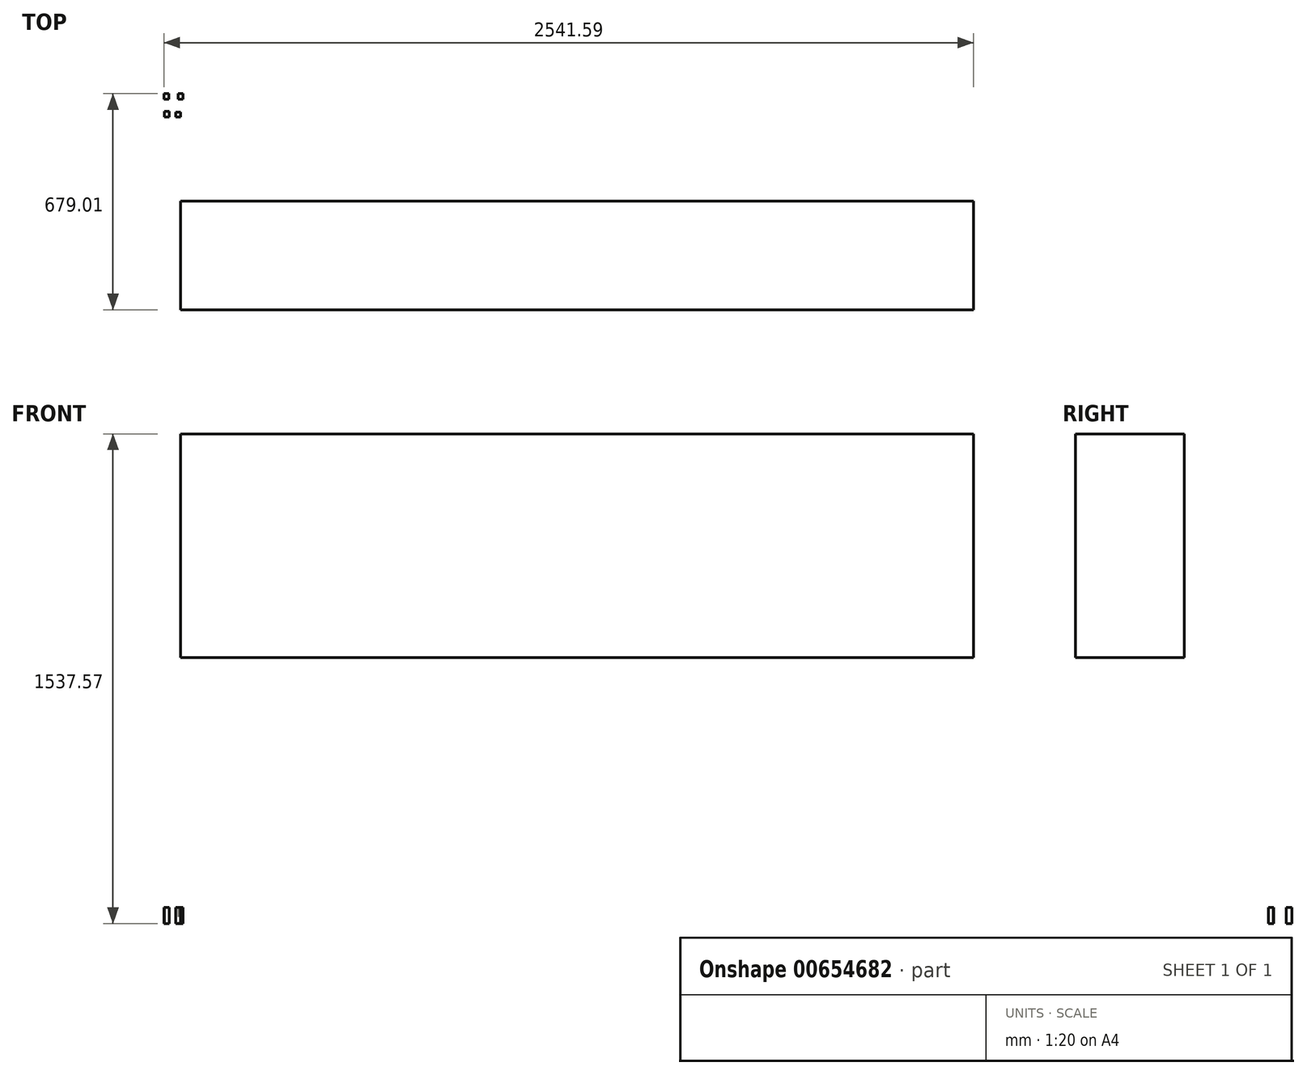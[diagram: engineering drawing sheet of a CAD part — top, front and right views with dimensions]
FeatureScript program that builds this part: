
annotation { "Feature Type Name" : "Feature", "Feature Type Description" : "" }
export const myFeature = defineFeature(function(context is Context, id is Id, definition is map)
    precondition{}
    {
        {
            var Q0;
            Q0=qCreatedBy(makeId("Top.planeOp"),FACE);
            var sketch = newSketch(context, id + "F0", { "sketchPlane" : qUnion([Q0])});
            skLineSegment(sketch, "E0.bottom", {"start": v(-51.02, -64.93) * mm, "end": v(-36.1, -64.93) * mm});
            skLineSegment(sketch, "E0.top", {"start": v(-51.02, -47.21) * mm, "end": v(-36.1, -47.21) * mm});
            skLineSegment(sketch, "E0.left", {"start": v(-51.02, -64.93) * mm, "end": v(-51.02, -47.21) * mm});
            skLineSegment(sketch, "E0.right", {"start": v(-36.1, -64.93) * mm, "end": v(-36.1, -47.21) * mm});
            skSolve(sketch);
        }
        {
            var Q0;
            Q0 = qSketchRegion(id + "F0", true);
            extrude(context, id + "F1", {"entities" : qUnion([Q0]), "depth" : 50.8 * mm, "offsetDistance" : 25.4 * mm});
        }
        {
            var Q0;
            Q0=qCreatedBy(makeId("Top.planeOp"),FACE);
            var sketch = newSketch(context, id + "F2", { "sketchPlane" : qUnion([Q0])});
            skLineSegment(sketch, "E1.bottom", {"start": v(-52.39, -8.86) * mm, "end": v(-37.46, -8.86) * mm});
            skLineSegment(sketch, "E1.top", {"start": v(-52.39, 8.86) * mm, "end": v(-37.46, 8.86) * mm});
            skLineSegment(sketch, "E1.left", {"start": v(-52.39, -8.86) * mm, "end": v(-52.39, 8.86) * mm});
            skLineSegment(sketch, "E1.right", {"start": v(-37.46, -8.86) * mm, "end": v(-37.46, 8.86) * mm});
            skSolve(sketch);
        }
        {
            var Q0;
            Q0=makeQuery(id+"F2.imprint","IMPRINT",FACE,{"disambiguationData":[TD([[makeQuery(id+"F2.imprint","IMPRINT",EDGE,{"derivedFrom":sQuery(id+"F2.wireOp",EDGE,"E1.bottom")}),1.0]])]});
            extrude(context, id + "F3", {"entities" : qUnion([Q0]), "depth" : 50.8 * mm, "offsetDistance" : 25.4 * mm});
        }
        {
            var Q0;
            Q0=qCreatedBy(makeId("Top.planeOp"),FACE);
            var sketch = newSketch(context, id + "F4", { "sketchPlane" : qUnion([Q0])});
            skLineSegment(sketch, "E2.bottom", {"start": v(-7.46, -8.86) * mm, "end": v(7.46, -8.86) * mm});
            skLineSegment(sketch, "E2.top", {"start": v(-7.46, 8.86) * mm, "end": v(7.46, 8.86) * mm});
            skLineSegment(sketch, "E2.left", {"start": v(-7.46, -8.86) * mm, "end": v(-7.46, 8.86) * mm});
            skLineSegment(sketch, "E2.right", {"start": v(7.46, -8.86) * mm, "end": v(7.46, 8.86) * mm});
            skSolve(sketch);
        }
        {
            var Q0;
            Q0=makeQuery(id+"F4.imprint","IMPRINT",FACE,{"disambiguationData":[TD([[makeQuery(id+"F4.imprint","IMPRINT",EDGE,{"derivedFrom":sQuery(id+"F4.wireOp",EDGE,"E2.bottom")}),1.0]])]});
            extrude(context, id + "F5", {"entities" : qUnion([Q0]), "depth" : 50.8 * mm, "offsetDistance" : 25.4 * mm});
        }
        {
            var Q0;
            Q0=qCreatedBy(makeId("Top.planeOp"),FACE);
            var sketch = newSketch(context, id + "F6", { "sketchPlane" : qUnion([Q0])});
            skLineSegment(sketch, "E3.bottom", {"start": v(-15, -48.88) * mm, "end": v(0, -48.88) * mm});
            skLineSegment(sketch, "E3.top", {"start": v(-15, -64.52) * mm, "end": v(0, -64.52) * mm});
            skLineSegment(sketch, "E3.left", {"start": v(-15, -48.88) * mm, "end": v(-15, -64.52) * mm});
            skLineSegment(sketch, "E3.right", {"start": v(0, -48.88) * mm, "end": v(0, -64.52) * mm});
            skSolve(sketch);
        }
        {
            var Q0;
            Q0=makeQuery(id+"F6.imprint","IMPRINT",FACE,{"disambiguationData":[TD([[makeQuery(id+"F6.imprint","IMPRINT",EDGE,{"derivedFrom":sQuery(id+"F6.wireOp",EDGE,"E3.bottom")}),-1.0]])]});
            extrude(context, id + "F7", {"entities" : qUnion([Q0]), "depth" : 50.8 * mm, "offsetDistance" : 25.4 * mm});
        }
        {
            var Q0;
            Q0=qCreatedBy(makeId("Top.planeOp"),FACE);
            var sketch = newSketch(context, id + "F8", { "sketchPlane" : qUnion([Q0])});
            skLineSegment(sketch, "E4.bottom", {"start": v(-69.36, 34.93) * mm, "end": v(-17.24, 34.93) * mm});
            skLineSegment(sketch, "E4.top", {"start": v(-69.36, -38.33) * mm, "end": v(-17.24, -38.33) * mm});
            skLineSegment(sketch, "E4.left", {"start": v(-69.36, 34.93) * mm, "end": v(-69.36, -38.33) * mm});
            skLineSegment(sketch, "E4.right", {"start": v(-17.24, 34.93) * mm, "end": v(-17.24, -38.33) * mm});
            skSolve(sketch);
        }
        {
            var Q0;
            Q0=makeQuery(id+"F8.imprint","IMPRINT",FACE,{"disambiguationData":[TD([[makeQuery(id+"F8.imprint","IMPRINT",EDGE,{"derivedFrom":sQuery(id+"F8.wireOp",EDGE,"E4.bottom")}),-1.0]])]});
            extrude(context, id + "F9", {"entities" : qUnion([Q0]), "operationType" : NewBodyOperationType.REMOVE, "oppositeDirection" : true, "depth" : 50.8 * mm, "offsetDistance" : 25.4 * mm});
        }
        {
            var Q0;
            Q0=qCreatedBy(makeId("Right.planeOp"),FACE);
            var sketch = newSketch(context, id + "F10", { "sketchPlane" : qUnion([Q0])});
            skLineSegment(sketch, "E5.bottom", {"start": v(-328.92, 835.1) * mm, "end": v(-670.15, 835.1) * mm});
            skLineSegment(sketch, "E5.top", {"start": v(-328.92, 1537.57) * mm, "end": v(-670.15, 1537.57) * mm});
            skLineSegment(sketch, "E5.left", {"start": v(-328.92, 835.1) * mm, "end": v(-328.92, 1537.57) * mm});
            skLineSegment(sketch, "E5.right", {"start": v(-670.15, 835.1) * mm, "end": v(-670.15, 1537.57) * mm});
            skSolve(sketch);
        }
        {
            var Q0;
            Q0 = qSketchRegion(id + "F10", true);
            extrude(context, id + "F11", {"entities" : qUnion([Q0]), "depth" : 2489.2 * mm, "offsetDistance" : 25.4 * mm});
        }
    });
